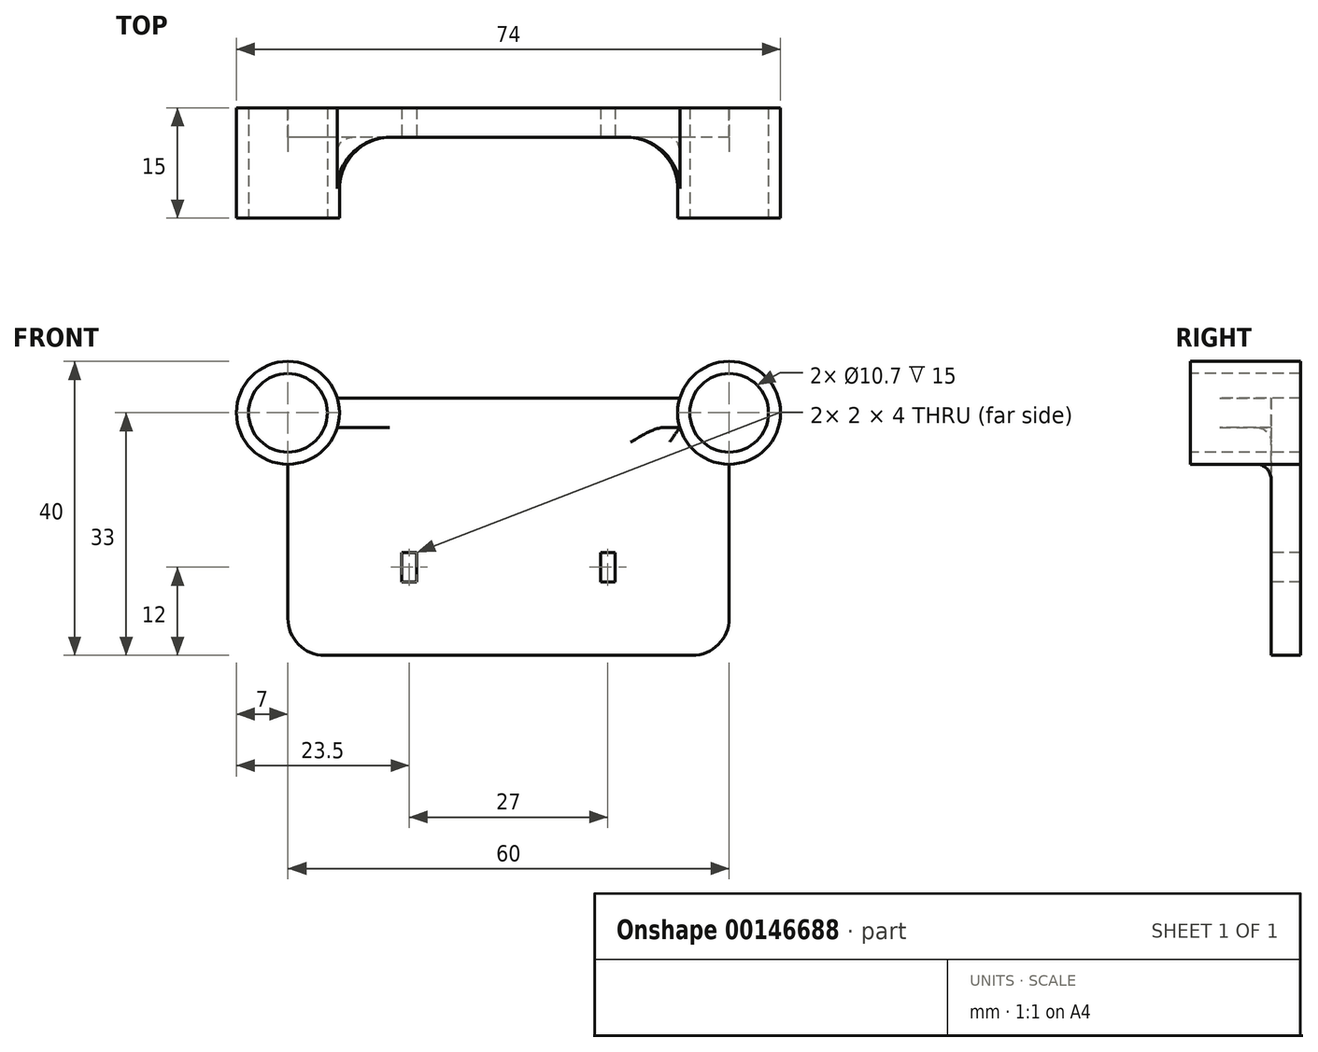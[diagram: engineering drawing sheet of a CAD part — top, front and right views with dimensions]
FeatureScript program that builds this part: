
annotation { "Feature Type Name" : "Feature", "Feature Type Description" : "" }
export const myFeature = defineFeature(function(context is Context, id is Id, definition is map)
    precondition{}
    {
        {
            var Q0;
            Q0=qCreatedBy(makeId("Front.planeOp"),FACE);
            cPlane(context, id + "F0", {"entities" : qUnion([Q0]), "cplaneType" : CPlaneType.OFFSET, "offset" : 0 * mm, "width" : 150 * mm, "height" : 150 * mm});
        }
        {
            var Q0;
            Q0=qCreatedBy(id+"F0.planeOp",FACE);
            var sketch = newSketch(context, id + "F1", { "sketchPlane" : qUnion([Q0])});
            skCircle(sketch, "E0", {"center": v(-30, 0) * mm, "radius": 7 * mm});
            skSolve(sketch);
        }
        {
            var Q0;
            Q0=qCreatedBy(id+"F0.planeOp",FACE);
            var sketch = newSketch(context, id + "F2", { "sketchPlane" : qUnion([Q0])});
            skCircle(sketch, "E1", {"center": v(30, 0) * mm, "radius": 7 * mm});
            skSolve(sketch);
        }
        {
            var Q0;
            Q0=qSketchRegion(id+"F1",true);
            var Q1;
            Q1=qSketchRegion(id+"F2",true);
            extrude(context, id + "F3", {"entities" : qUnion([Q0, Q1]), "oppositeDirection" : true, "depth" : 15 * mm});
        }
        {
            var Q0;
            Q0=qCreatedBy(id+"F0.planeOp",FACE);
            var sketch = newSketch(context, id + "F4", { "sketchPlane" : qUnion([Q0])});
            skCircle(sketch, "E2", {"center": v(-30, 0) * mm, "radius": 5.35 * mm});
            skSolve(sketch);
        }
        {
            var Q0;
            Q0=qCreatedBy(id+"F0.planeOp",FACE);
            var sketch = newSketch(context, id + "F5", { "sketchPlane" : qUnion([Q0])});
            skCircle(sketch, "E3", {"center": v(30, 0) * mm, "radius": 5.35 * mm});
            skSolve(sketch);
        }
        {
            var Q0;
            Q0=qSketchRegion(id+"F4",true);
            var Q1;
            Q1=qSketchRegion(id+"F5",true);
            extrude(context, id + "F6", {"entities" : qUnion([Q0, Q1]), "oppositeDirection" : true, "depth" : 30 * mm});
        }
        {
            var Q0;
            Q0=qCreatedBy(makeId("Right.planeOp"),FACE);
            var sketch = newSketch(context, id + "F7", { "sketchPlane" : qUnion([Q0])});
            skLineSegment(sketch, "E4.bottom", {"start": v(11, 2) * mm, "end": v(15, 2) * mm});
            skLineSegment(sketch, "E4.top", {"start": v(11, -2) * mm, "end": v(15, -2) * mm});
            skLineSegment(sketch, "E4.left", {"start": v(11, 2) * mm, "end": v(11, -2) * mm});
            skLineSegment(sketch, "E4.right", {"start": v(15, 2) * mm, "end": v(15, -2) * mm});
            skSolve(sketch);
        }
        {
            var Q0;
            Q0=qSketchRegion(id+"F7",true);
            extrude(context, id + "F8", {"entities" : qUnion([Q0]), "endBound" : BoundingType.SYMMETRIC, "depth" : 50 * mm});
        }
        {
            var Q0;
            Q0=makeQuery(id+"F3.opExtrude","SWEPT_BODY",BODY,{"disambiguationData":[OSD([sQuery(id+"F1.wireOp",EDGE,"E0")])]});
            var Q1;
            Q1=makeQuery(id+"F3.opExtrude","SWEPT_BODY",BODY,{"disambiguationData":[OSD([sQuery(id+"F2.wireOp",EDGE,"E1")])]});
            var Q2;
            Q2=makeQuery(id+"F8.opExtrude","SWEPT_BODY",BODY,{"disambiguationData":[OSD([sQuery(id+"F7.wireOp",EDGE,"E4.bottom"),sQuery(id+"F7.wireOp",EDGE,"E4.top"),sQuery(id+"F7.wireOp",EDGE,"E4.left"),sQuery(id+"F7.wireOp",EDGE,"E4.right")])]});
            booleanBodies(context, id + "F9", {"operationType" : BooleanOperationType.UNION, "tools" : qUnion([Q0, Q1, Q2])});
        }
        {
            var Q0;
            Q0=makeQuery(id+"F9.opBoolean","INTERSECT",EDGE,{"derivedFrom":[makeQuery(id+"F3.opExtrude","SWEPT_FACE",FACE,{"disambiguationData":[OSD([sQuery(id+"F1.wireOp",EDGE,"E0")])]}),makeQuery(id+"F8.opExtrude","SWEPT_FACE",FACE,{"disambiguationData":[OSD([sQuery(id+"F7.wireOp",EDGE,"E4.left")])]})]});
            var Q1;
            Q1=makeQuery(id+"F9.opBoolean","INTERSECT",EDGE,{"derivedFrom":[makeQuery(id+"F3.opExtrude","SWEPT_FACE",FACE,{"disambiguationData":[OSD([sQuery(id+"F2.wireOp",EDGE,"E1")])]}),makeQuery(id+"F8.opExtrude","SWEPT_FACE",FACE,{"disambiguationData":[OSD([sQuery(id+"F7.wireOp",EDGE,"E4.left")])]})]});
            var Q2;
            Q2=makeQuery(id+"F9.opBoolean","INTERSECT",EDGE,{"derivedFrom":[makeQuery(id+"F3.opExtrude","SWEPT_FACE",FACE,{"disambiguationData":[OSD([sQuery(id+"F2.wireOp",EDGE,"E1")])]}),makeQuery(id+"F8.opExtrude","SWEPT_FACE",FACE,{"disambiguationData":[OSD([sQuery(id+"F7.wireOp",EDGE,"E4.right")])]})]});
            var Q3;
            Q3=makeQuery(id+"F9.opBoolean","INTERSECT",EDGE,{"derivedFrom":[makeQuery(id+"F3.opExtrude","SWEPT_FACE",FACE,{"disambiguationData":[OSD([sQuery(id+"F1.wireOp",EDGE,"E0")])]}),makeQuery(id+"F8.opExtrude","SWEPT_FACE",FACE,{"disambiguationData":[OSD([sQuery(id+"F7.wireOp",EDGE,"E4.right")])]})]});
            fillet(context, id + "F10", {"entities" : qUnion([Q0, Q1, Q2, Q3]), "radius" : 7 * mm, "tangentPropagation" : true, "allowEdgeOverflow" : false});
        }
        {
            var Q0;
            Q0=qCreatedBy(makeId("Right.planeOp"),FACE);
            var sketch = newSketch(context, id + "F11", { "sketchPlane" : qUnion([Q0])});
            skLineSegment(sketch, "E5.bottom", {"start": v(11, -2) * mm, "end": v(15, -2) * mm});
            skLineSegment(sketch, "E5.top", {"start": v(11, -33) * mm, "end": v(15, -33) * mm});
            skLineSegment(sketch, "E5.left", {"start": v(11, -2) * mm, "end": v(11, -33) * mm});
            skLineSegment(sketch, "E5.right", {"start": v(15, -2) * mm, "end": v(15, -33) * mm});
            skSolve(sketch);
        }
        {
            var Q0;
            Q0=makeQuery(id+"F11.imprint","IMPRINT",FACE,{"disambiguationData":[TD([[makeQuery(id+"F11.imprint","IMPRINT",EDGE,{"derivedFrom":sQuery(id+"F11.wireOp",EDGE,"E5.bottom")}),-1.0]])]});
            extrude(context, id + "F12", {"entities" : qUnion([Q0]), "endBound" : BoundingType.SYMMETRIC, "depth" : 60 * mm});
        }
        {
            var Q0;
            Q0=makeQuery(id+"F3.opExtrude","SWEPT_BODY",BODY,{"disambiguationData":[OSD([sQuery(id+"F1.wireOp",EDGE,"E0")])]});
            var Q1;
            Q1=makeQuery(id+"F12.opExtrude","SWEPT_BODY",BODY,{"disambiguationData":[OSD([sQuery(id+"F11.wireOp",EDGE,"E5.bottom"),sQuery(id+"F11.wireOp",EDGE,"E5.top"),sQuery(id+"F11.wireOp",EDGE,"E5.left"),sQuery(id+"F11.wireOp",EDGE,"E5.right")])]});
            booleanBodies(context, id + "F13", {"operationType" : BooleanOperationType.UNION, "tools" : qUnion([Q0, Q1])});
        }
        {
            var Q0;
            Q0=makeQuery(id+"F13.opBoolean","INTERSECT",EDGE,{"derivedFrom":[makeQuery(id+"F3.opExtrude","SWEPT_FACE",FACE,{"disambiguationData":[OSD([sQuery(id+"F1.wireOp",EDGE,"E0")])]}),makeQuery(id+"F12.opExtrude","SWEPT_FACE",FACE,{"disambiguationData":[OSD([sQuery(id+"F11.wireOp",EDGE,"E5.right")])]})]});
            var Q1;
            {var subQ1=sQuery(id+"F1.wireOp",EDGE,"E0");var subQ2=sQuery(id+"F11.wireOp",EDGE,"E5.right");Q1=makeQuery(id+"F13.opBoolean","SPLIT",EDGE,{"disambiguationData":[TD([makeQuery(id+"F3.opExtrude","SWEPT_FACE",FACE,{"disambiguationData":[OSD([subQ1])]})])],"derivedFrom":makeQuery(id+"F12.opExtrude","SWEPT_EDGE",EDGE,{"disambiguationData":[OSD([sQuery(id+"F11.wireOp",EDGE,"E5.bottom"),subQ2])]})});}
            var Q2;
            {var subQ1=sQuery(id+"F2.wireOp",EDGE,"E1");var subQ2=sQuery(id+"F11.wireOp",EDGE,"E5.right");Q2=makeQuery(id+"F13.opBoolean","SPLIT",EDGE,{"disambiguationData":[TD([makeQuery(id+"F3.opExtrude","SWEPT_FACE",FACE,{"disambiguationData":[OSD([subQ1])]})])],"derivedFrom":makeQuery(id+"F12.opExtrude","SWEPT_EDGE",EDGE,{"disambiguationData":[OSD([sQuery(id+"F11.wireOp",EDGE,"E5.bottom"),subQ2])]})});}
            var Q3;
            Q3=makeQuery(id+"F13.opBoolean","INTERSECT",EDGE,{"derivedFrom":[makeQuery(id+"F3.opExtrude","SWEPT_FACE",FACE,{"disambiguationData":[OSD([sQuery(id+"F2.wireOp",EDGE,"E1")])]}),makeQuery(id+"F12.opExtrude","SWEPT_FACE",FACE,{"disambiguationData":[OSD([sQuery(id+"F11.wireOp",EDGE,"E5.right")])]})]});
            var Q4;
            {var subQ1=sQuery(id+"F2.wireOp",EDGE,"E1");var subQ2=sQuery(id+"F11.wireOp",EDGE,"E5.left");Q4=makeQuery(id+"F13.opBoolean","SPLIT",EDGE,{"disambiguationData":[TD([makeQuery(id+"F3.opExtrude","SWEPT_FACE",FACE,{"disambiguationData":[OSD([subQ1])]})])],"derivedFrom":makeQuery(id+"F12.opExtrude","SWEPT_EDGE",EDGE,{"disambiguationData":[OSD([sQuery(id+"F11.wireOp",EDGE,"E5.bottom"),subQ2])]})});}
            var Q5;
            Q5=makeQuery(id+"F13.opBoolean","INTERSECT",EDGE,{"derivedFrom":[makeQuery(id+"F3.opExtrude","SWEPT_FACE",FACE,{"disambiguationData":[OSD([sQuery(id+"F2.wireOp",EDGE,"E1")])]}),makeQuery(id+"F12.opExtrude","SWEPT_FACE",FACE,{"disambiguationData":[OSD([sQuery(id+"F11.wireOp",EDGE,"E5.left")])]})]});
            var Q6;
            {var subQ1=sQuery(id+"F1.wireOp",EDGE,"E0");var subQ2=sQuery(id+"F11.wireOp",EDGE,"E5.left");Q6=makeQuery(id+"F13.opBoolean","SPLIT",EDGE,{"disambiguationData":[TD([makeQuery(id+"F3.opExtrude","SWEPT_FACE",FACE,{"disambiguationData":[OSD([subQ1])]})])],"derivedFrom":makeQuery(id+"F12.opExtrude","SWEPT_EDGE",EDGE,{"disambiguationData":[OSD([sQuery(id+"F11.wireOp",EDGE,"E5.bottom"),subQ2])]})});}
            var Q7;
            Q7=makeQuery(id+"F13.opBoolean","INTERSECT",EDGE,{"derivedFrom":[makeQuery(id+"F3.opExtrude","SWEPT_FACE",FACE,{"disambiguationData":[OSD([sQuery(id+"F1.wireOp",EDGE,"E0")])]}),makeQuery(id+"F12.opExtrude","SWEPT_FACE",FACE,{"disambiguationData":[OSD([sQuery(id+"F11.wireOp",EDGE,"E5.left")])]})]});
            fillet(context, id + "F14", {"entities" : qUnion([Q0, Q1, Q2, Q3, Q4, Q5, Q6, Q7]), "radius" : 2 * mm, "tangentPropagation" : true, "allowEdgeOverflow" : false});
        }
        {
            var Q0;
            Q0=makeQuery(id+"F12.opExtrude","CAP_EDGE",EDGE,{"disambiguationData":[OSD([sQuery(id+"F11.wireOp",EDGE,"E5.top")])],"isStart":false});
            var Q1;
            Q1=makeQuery(id+"F12.opExtrude","CAP_EDGE",EDGE,{"disambiguationData":[OSD([sQuery(id+"F11.wireOp",EDGE,"E5.top")])],"isStart":true});
            fillet(context, id + "F15", {"entities" : qUnion([Q0, Q1]), "radius" : 5 * mm, "tangentPropagation" : true, "allowEdgeOverflow" : false});
        }
        {
            var Q0;
            Q0=makeQuery(id+"F6.opExtrude","SWEPT_BODY",BODY,{"disambiguationData":[OSD([sQuery(id+"F4.wireOp",EDGE,"E2")])]});
            var Q1;
            Q1=makeQuery(id+"F6.opExtrude","SWEPT_BODY",BODY,{"disambiguationData":[OSD([sQuery(id+"F5.wireOp",EDGE,"E3")])]});
            var Q2;
            Q2=makeQuery(id+"F3.opExtrude","SWEPT_BODY",BODY,{"disambiguationData":[OSD([sQuery(id+"F1.wireOp",EDGE,"E0")])]});
            booleanBodies(context, id + "F16", {"operationType" : BooleanOperationType.SUBTRACTION, "tools" : qUnion([Q0, Q1]), "targets" : qUnion([Q2])});
        }
        {
            var Q0;
            Q0=makeQuery(id+"F13.opBoolean","MERGE",FACE,{"derivedFrom":[makeQuery(id+"F8.opExtrude","SWEPT_FACE",FACE,{"disambiguationData":[OSD([sQuery(id+"F7.wireOp",EDGE,"E4.left")])]}),makeQuery(id+"F12.opExtrude","SWEPT_FACE",FACE,{"disambiguationData":[OSD([sQuery(id+"F11.wireOp",EDGE,"E5.left")])]})]});
            var sketch = newSketch(context, id + "F17", { "sketchPlane" : qUnion([Q0])});
            skLineSegment(sketch, "E6.bottom", {"start": v(12.5, -19) * mm, "end": v(14.5, -19) * mm});
            skLineSegment(sketch, "E6.top", {"start": v(12.5, -23) * mm, "end": v(14.5, -23) * mm});
            skLineSegment(sketch, "E6.left", {"start": v(12.5, -19) * mm, "end": v(12.5, -23) * mm});
            skLineSegment(sketch, "E6.right", {"start": v(14.5, -19) * mm, "end": v(14.5, -23) * mm});
            skSolve(sketch);
        }
        {
            var Q0;
            Q0=makeQuery(id+"F17.imprint","IMPRINT",FACE,{"disambiguationData":[TD([[makeQuery(id+"F17.imprint","IMPRINT",EDGE,{"derivedFrom":sQuery(id+"F17.wireOp",EDGE,"E6.bottom")}),1.0]])]});
            var sketch = newSketch(context, id + "F18", { "sketchPlane" : qUnion([Q0])});
            skLineSegment(sketch, "E7.bottom", {"start": v(-14.5, -19) * mm, "end": v(-12.5, -19) * mm});
            skLineSegment(sketch, "E7.top", {"start": v(-14.5, -23) * mm, "end": v(-12.5, -23) * mm});
            skLineSegment(sketch, "E7.left", {"start": v(-14.5, -19) * mm, "end": v(-14.5, -23) * mm});
            skLineSegment(sketch, "E7.right", {"start": v(-12.5, -19) * mm, "end": v(-12.5, -23) * mm});
            skSolve(sketch);
        }
        {
            var Q0;
            Q0=qSketchRegion(id+"F17",true);
            var Q1;
            Q1=qSketchRegion(id+"F18",true);
            extrude(context, id + "F19", {"entities" : qUnion([Q0, Q1]), "oppositeDirection" : true, "depth" : 25 * mm});
        }
        {
            var Q0;
            Q0=makeQuery(id+"F19.opExtrude","SWEPT_BODY",BODY,{"disambiguationData":[OSD([sQuery(id+"F17.wireOp",EDGE,"E6.bottom"),sQuery(id+"F17.wireOp",EDGE,"E6.top"),sQuery(id+"F17.wireOp",EDGE,"E6.left"),sQuery(id+"F17.wireOp",EDGE,"E6.right")])]});
            var Q1;
            Q1=makeQuery(id+"F19.opExtrude","SWEPT_BODY",BODY,{"disambiguationData":[OSD([sQuery(id+"F18.wireOp",EDGE,"E7.bottom"),sQuery(id+"F18.wireOp",EDGE,"E7.top"),sQuery(id+"F18.wireOp",EDGE,"E7.left"),sQuery(id+"F18.wireOp",EDGE,"E7.right")])]});
            var Q2;
            Q2=makeQuery(id+"F3.opExtrude","SWEPT_BODY",BODY,{"disambiguationData":[OSD([sQuery(id+"F1.wireOp",EDGE,"E0")])]});
            booleanBodies(context, id + "F20", {"operationType" : BooleanOperationType.SUBTRACTION, "tools" : qUnion([Q0, Q1]), "targets" : qUnion([Q2])});
        }
    });
